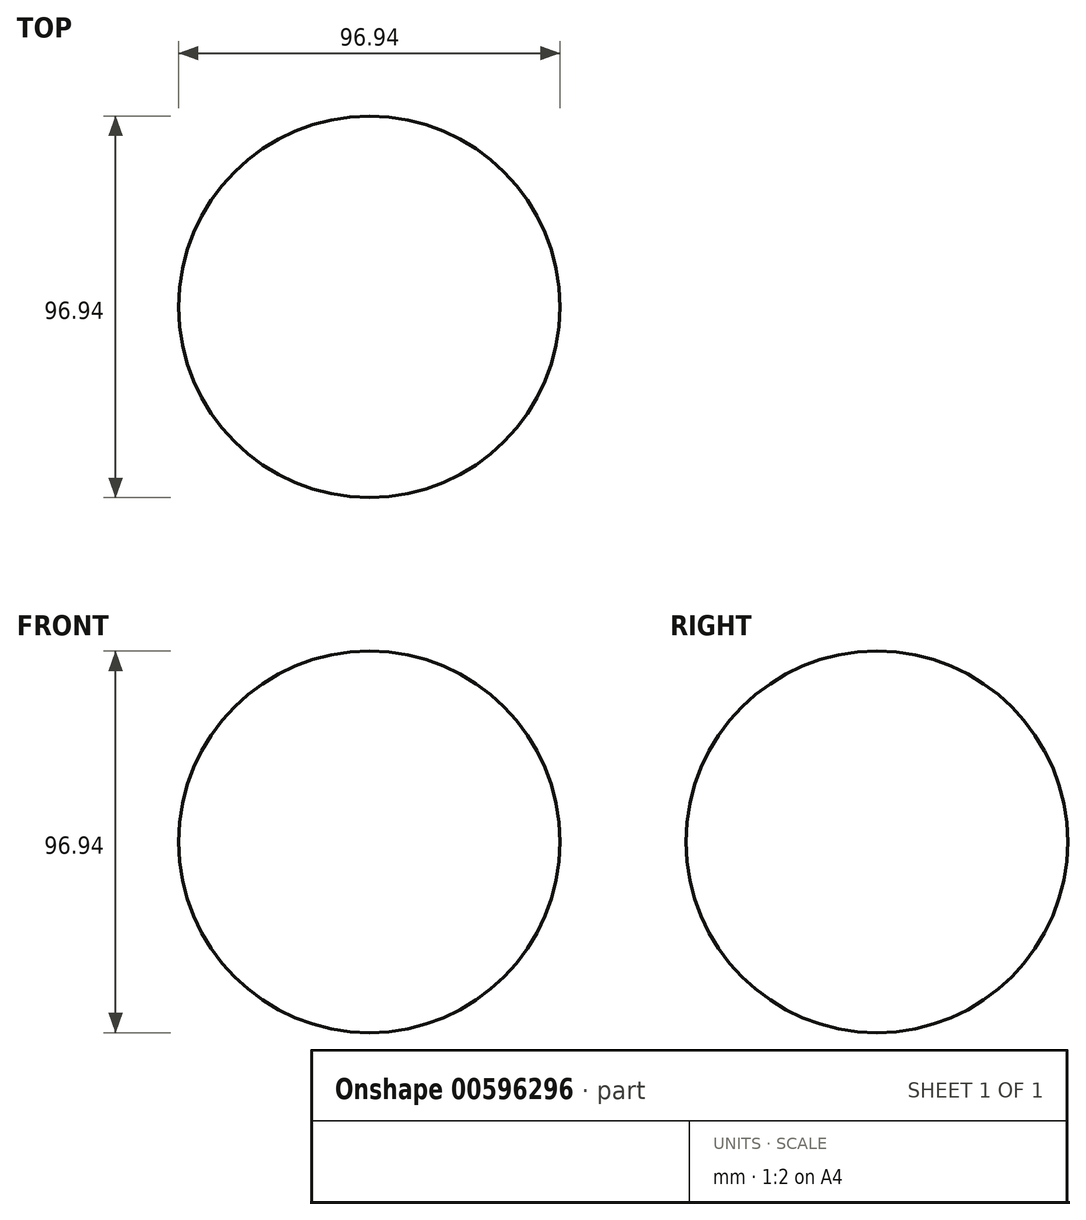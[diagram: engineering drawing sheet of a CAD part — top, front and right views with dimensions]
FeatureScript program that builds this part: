
annotation { "Feature Type Name" : "Feature", "Feature Type Description" : "" }
export const myFeature = defineFeature(function(context is Context, id is Id, definition is map)
    precondition{}
    {
        {
            var Q0;
            Q0=qCreatedBy(makeId("Front.planeOp"),FACE);
            var sketch = newSketch(context, id + "F0", { "sketchPlane" : qUnion([Q0])});
            skPoint(sketch, "E0.center.orphan", {"position": v(0, -2.44) * mm});
            skArc(sketch, "E1", {"start": v(0, -48.47) * mm, "mid": v(48.47, 0) * mm, "end": v(0, 48.47) * mm});
            skLineSegment(sketch, "E2", {"start": v(0, 48.47) * mm, "end": v(0, -56.19) * mm});
            skSolve(sketch);
        }
        {
            var Q0;
            Q0 = qSketchRegion(id + "F0", true);
            var Q1;
            Q1=sQuery(id+"F0.wireOp",EDGE,"E2");
            revolve(context, id + "F1", {"entities" : qUnion([Q0]), "axis" : qUnion([Q1]), "revolveType" : RevolveType.FULL});
        }
    });
